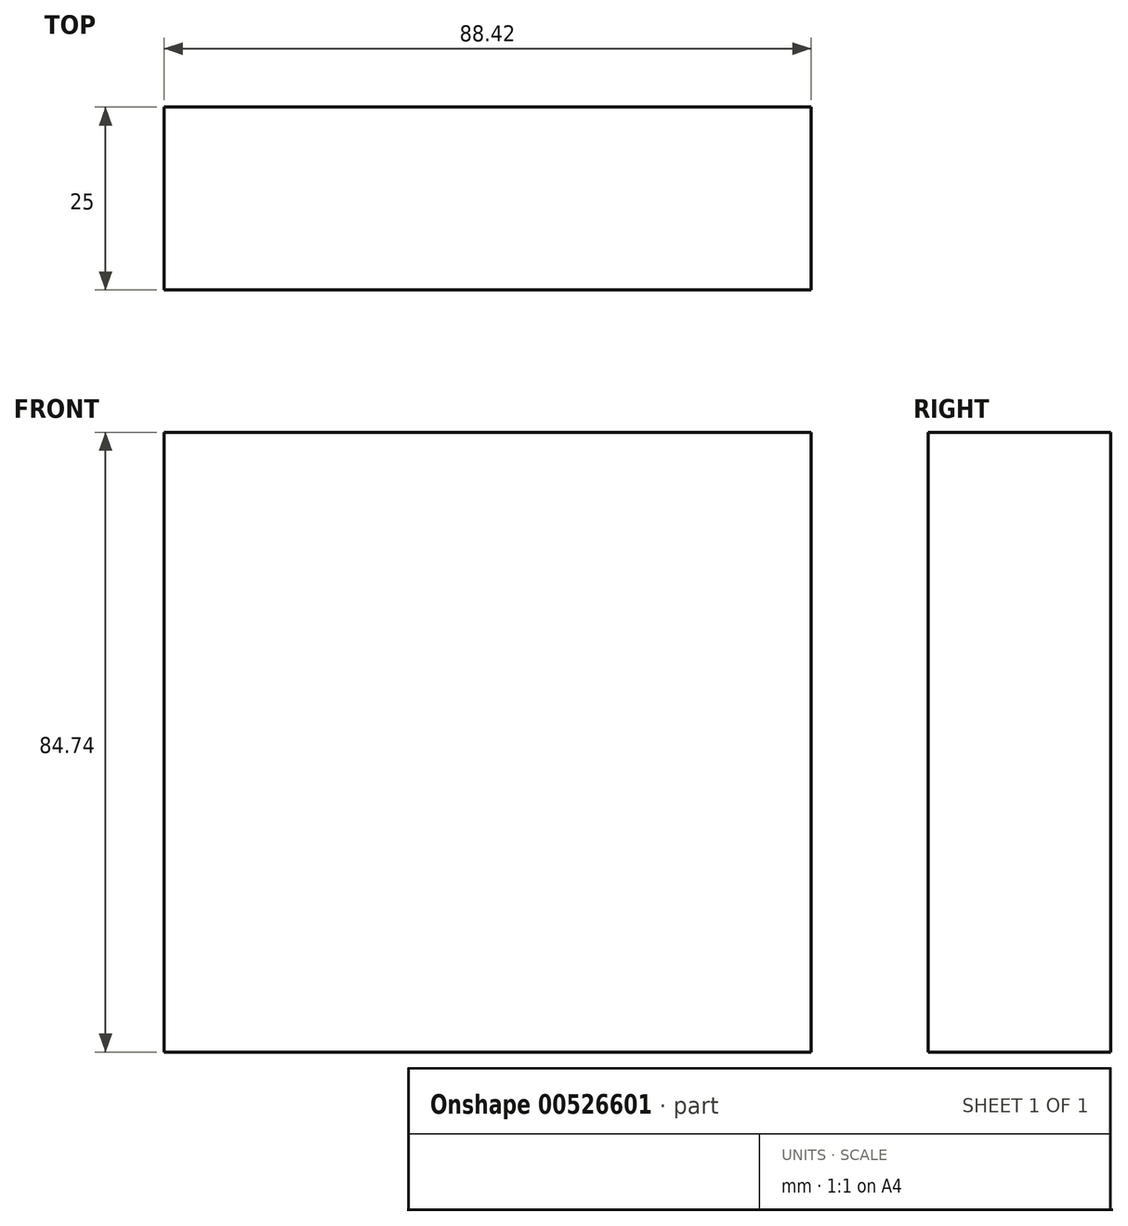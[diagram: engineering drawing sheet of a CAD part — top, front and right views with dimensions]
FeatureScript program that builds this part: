
annotation { "Feature Type Name" : "Feature", "Feature Type Description" : "" }
export const myFeature = defineFeature(function(context is Context, id is Id, definition is map)
    precondition{}
    {
        {
            var Q0;
            Q0=qCreatedBy(makeId("Front.planeOp"),FACE);
            var sketch = newSketch(context, id + "F0", { "sketchPlane" : qUnion([Q0])});
            skLineSegment(sketch, "E0.bottom", {"start": v(-47.17, 57.38) * mm, "end": v(41.25, 57.38) * mm});
            skLineSegment(sketch, "E0.top", {"start": v(-47.17, -27.36) * mm, "end": v(41.25, -27.36) * mm});
            skLineSegment(sketch, "E0.left", {"start": v(-47.17, 57.38) * mm, "end": v(-47.17, -27.36) * mm});
            skLineSegment(sketch, "E0.right", {"start": v(41.25, 57.38) * mm, "end": v(41.25, -27.36) * mm});
            skSolve(sketch);
        }
        {
            var Q0;
            Q0 = qSketchRegion(id + "F0", true);
            extrude(context, id + "F1", {"entities" : qUnion([Q0]), "depth" : 25 * mm, "offsetDistance" : 25 * mm});
        }
    });
